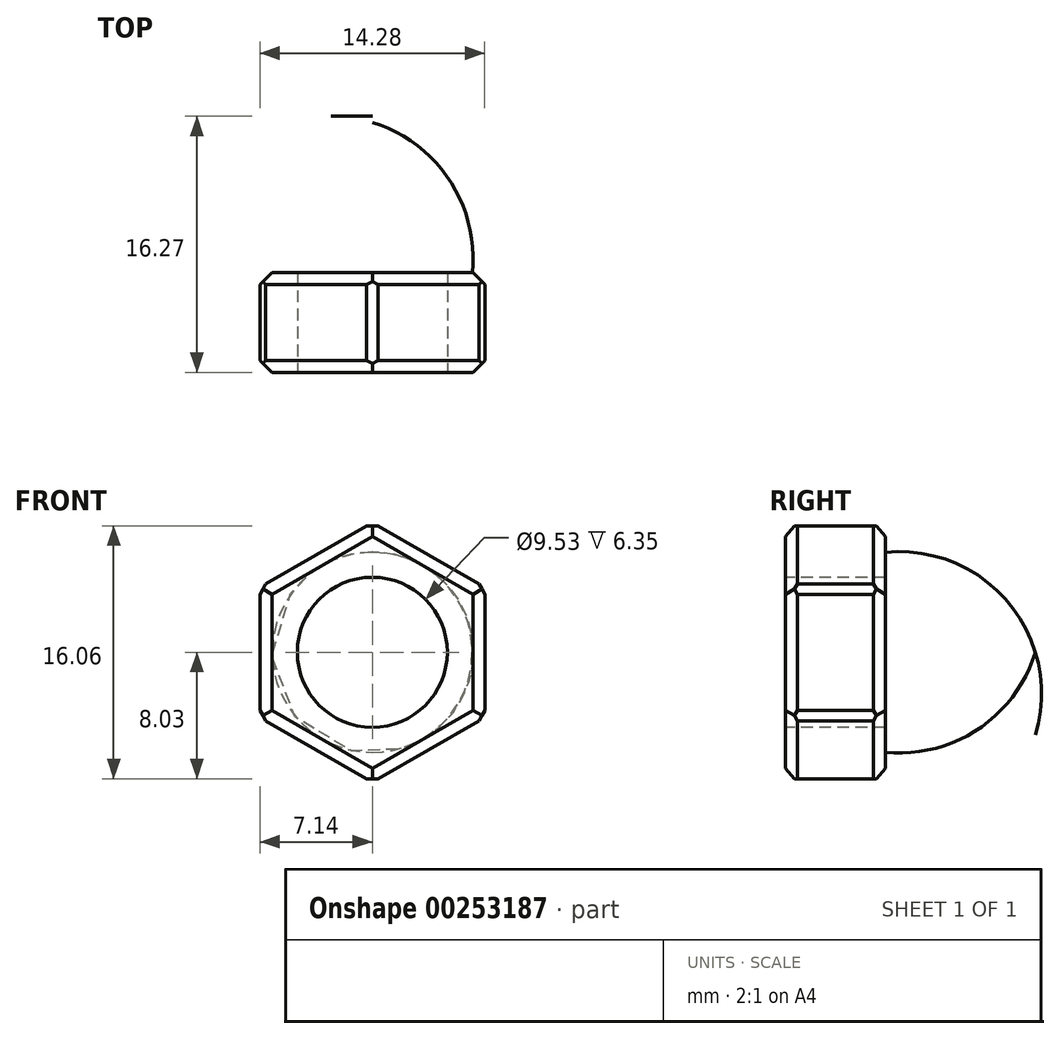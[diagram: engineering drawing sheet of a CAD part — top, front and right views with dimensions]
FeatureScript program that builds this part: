
annotation { "Feature Type Name" : "Feature", "Feature Type Description" : "" }
export const myFeature = defineFeature(function(context is Context, id is Id, definition is map)
    precondition{}
    {
        {
            var Q0;
            Q0=qCreatedBy(makeId("Front.planeOp"),FACE);
            var sketch = newSketch(context, id + "F0", { "sketchPlane" : qUnion([Q0])});
            skCircle(sketch, "E0.cCircle", {"center": v(0, 0) * mm, "radius": 7.14 * mm, "construction": true});
            skLineSegment(sketch, "E0.0", {"start": v(-7.14, -4.12) * mm, "end": v(-7.14, 4.12) * mm});
            skLineSegment(sketch, "E0.1", {"start": v(-7.14, 4.12) * mm, "end": v(0, 8.25) * mm});
            skLineSegment(sketch, "E0.2", {"start": v(0, 8.25) * mm, "end": v(7.14, 4.12) * mm});
            skLineSegment(sketch, "E0.3", {"start": v(7.14, 4.12) * mm, "end": v(7.14, -4.12) * mm});
            skLineSegment(sketch, "E0.4", {"start": v(7.14, -4.12) * mm, "end": v(0, -8.25) * mm});
            skLineSegment(sketch, "E0.5", {"start": v(0, -8.25) * mm, "end": v(-7.14, -4.12) * mm});
            skPoint(sketch, "E0.0.midPoint", {"position": v(-7.14, 0) * mm});
            skSolve(sketch);
        }
        {
            var Q0;
            Q0=makeQuery(id+"F0.imprint","IMPRINT",FACE,{"disambiguationData":[TD([[makeQuery(id+"F0.imprint","IMPRINT",EDGE,{"derivedFrom":sQuery(id+"F0.wireOp",EDGE,"E0.0")}),-1.0]])]});
            extrude(context, id + "F1", {"entities" : qUnion([Q0]), "depth" : 6.35 * mm, "symmetric" : true});
        }
        {
            var Q0;
            Q0=makeQuery(id+"F1.opExtrude","CAP_FACE",FACE,{"disambiguationData":[OSD([sQuery(id+"F0.wireOp",EDGE,"E0.0"),sQuery(id+"F0.wireOp",EDGE,"E0.1"),sQuery(id+"F0.wireOp",EDGE,"E0.2"),sQuery(id+"F0.wireOp",EDGE,"E0.3"),sQuery(id+"F0.wireOp",EDGE,"E0.4"),sQuery(id+"F0.wireOp",EDGE,"E0.5")])],"isStart":false});
            var sketch = newSketch(context, id + "F2", { "sketchPlane" : qUnion([Q0])});
            skCircle(sketch, "E1", {"center": v(0, 0) * mm, "radius": 4.76 * mm});
            skSolve(sketch);
        }
        {
            var Q0;
            Q0=qSketchRegion(id+"F2",true);
            extrude(context, id + "F3", {"entities" : qUnion([Q0]), "operationType" : NewBodyOperationType.REMOVE, "oppositeDirection" : true, "depth" : 25 * mm});
        }
        {
            var Q0;
            Q0=makeQuery(id+"F1.opExtrude","SWEPT_EDGE",EDGE,{"disambiguationData":[OSD([sQuery(id+"F0.wireOp",EDGE,"E0.1"),sQuery(id+"F0.wireOp",EDGE,"E0.2")])]});
            var Q1;
            Q1=makeQuery(id+"F1.opExtrude","SWEPT_EDGE",EDGE,{"disambiguationData":[OSD([sQuery(id+"F0.wireOp",EDGE,"E0.2"),sQuery(id+"F0.wireOp",EDGE,"E0.3")])]});
            var Q2;
            Q2=makeQuery(id+"F1.opExtrude","SWEPT_EDGE",EDGE,{"disambiguationData":[OSD([sQuery(id+"F0.wireOp",EDGE,"E0.3"),sQuery(id+"F0.wireOp",EDGE,"E0.4")])]});
            var Q3;
            Q3=makeQuery(id+"F1.opExtrude","SWEPT_EDGE",EDGE,{"disambiguationData":[OSD([sQuery(id+"F0.wireOp",EDGE,"E0.4"),sQuery(id+"F0.wireOp",EDGE,"E0.5")])]});
            var Q4;
            Q4=makeQuery(id+"F1.opExtrude","SWEPT_EDGE",EDGE,{"disambiguationData":[OSD([sQuery(id+"F0.wireOp",EDGE,"E0.0"),sQuery(id+"F0.wireOp",EDGE,"E0.5")])]});
            var Q5;
            Q5=makeQuery(id+"F1.opExtrude","SWEPT_EDGE",EDGE,{"disambiguationData":[OSD([sQuery(id+"F0.wireOp",EDGE,"E0.0"),sQuery(id+"F0.wireOp",EDGE,"E0.1")])]});
            chamfer(context, id + "F4", {"entities" : qUnion([Q0, Q1, Q2, Q3, Q4, Q5]), "width" : 0.76 * mm, "tangentPropagation" : true});
        }
        {
            var Q0;
            Q0=makeQuery(id+"F1.opExtrude","CAP_EDGE",EDGE,{"disambiguationData":[OSD([sQuery(id+"F0.wireOp",EDGE,"E0.5")])],"isStart":false});
            var Q1;
            Q1=makeQuery(id+"F1.opExtrude","CAP_EDGE",EDGE,{"disambiguationData":[OSD([sQuery(id+"F0.wireOp",EDGE,"E0.4")])],"isStart":false});
            var Q2;
            Q2=makeQuery(id+"F1.opExtrude","CAP_EDGE",EDGE,{"disambiguationData":[OSD([sQuery(id+"F0.wireOp",EDGE,"E0.3")])],"isStart":false});
            var Q3;
            Q3=makeQuery(id+"F1.opExtrude","CAP_EDGE",EDGE,{"disambiguationData":[OSD([sQuery(id+"F0.wireOp",EDGE,"E0.2")])],"isStart":false});
            var Q4;
            Q4=makeQuery(id+"F1.opExtrude","CAP_EDGE",EDGE,{"disambiguationData":[OSD([sQuery(id+"F0.wireOp",EDGE,"E0.1")])],"isStart":false});
            var Q5;
            Q5=makeQuery(id+"F1.opExtrude","CAP_EDGE",EDGE,{"disambiguationData":[OSD([sQuery(id+"F0.wireOp",EDGE,"E0.0")])],"isStart":false});
            chamfer(context, id + "F5", {"entities" : qUnion([Q0, Q1, Q2, Q3, Q4, Q5]), "width" : 0.76 * mm, "tangentPropagation" : true});
        }
        {
            var Q0;
            Q0=makeQuery(id+"F1.opExtrude","CAP_EDGE",EDGE,{"disambiguationData":[OSD([sQuery(id+"F0.wireOp",EDGE,"E0.5")])],"isStart":true});
            var Q1;
            Q1=makeQuery(id+"F1.opExtrude","CAP_EDGE",EDGE,{"disambiguationData":[OSD([sQuery(id+"F0.wireOp",EDGE,"E0.4")])],"isStart":true});
            var Q2;
            Q2=makeQuery(id+"F1.opExtrude","CAP_EDGE",EDGE,{"disambiguationData":[OSD([sQuery(id+"F0.wireOp",EDGE,"E0.3")])],"isStart":true});
            var Q3;
            Q3=makeQuery(id+"F1.opExtrude","CAP_EDGE",EDGE,{"disambiguationData":[OSD([sQuery(id+"F0.wireOp",EDGE,"E0.2")])],"isStart":true});
            var Q4;
            Q4=makeQuery(id+"F1.opExtrude","CAP_EDGE",EDGE,{"disambiguationData":[OSD([sQuery(id+"F0.wireOp",EDGE,"E0.1")])],"isStart":true});
            var Q5;
            Q5=makeQuery(id+"F1.opExtrude","CAP_EDGE",EDGE,{"disambiguationData":[OSD([sQuery(id+"F0.wireOp",EDGE,"E0.0")])],"isStart":true});
            chamfer(context, id + "F6", {"entities" : qUnion([Q0, Q1, Q2, Q3, Q4, Q5]), "width" : 0.76 * mm, "tangentPropagation" : true});
        }
        {
            var Q0;
            Q0=qCreatedBy(makeId("Top.planeOp"),FACE);
            var sketch = newSketch(context, id + "F7", { "sketchPlane" : qUnion([Q0])});
            skLineSegment(sketch, "E2", {"start": v(0, 3.18) * mm, "end": v(0, 12.7) * mm});
            skLineSegment(sketch, "E3", {"start": v(0, 3.18) * mm, "end": v(6.35, 3.18) * mm});
            skArc(sketch, "E4", {"start": v(6.35, 3.18) * mm, "mid": v(4.88, 9.07) * mm, "end": v(0, 12.7) * mm});
            skSolve(sketch);
        }
        {
            var Q0;
            Q0=makeQuery(id+"F7.imprint","IMPRINT",FACE,{"disambiguationData":[TD([[makeQuery(id+"F7.imprint","IMPRINT",EDGE,{"derivedFrom":sQuery(id+"F7.wireOp",EDGE,"E2")}),-1.0]])]});
            var Q1;
            Q1=sQuery(id+"F7.wireOp",EDGE,"E2");
            revolve(context, id + "F8", {"operationType" : NewBodyOperationType.ADD, "entities" : qUnion([Q0]), "axis" : qUnion([Q1]), "revolveType" : RevolveType.FULL});
        }
    });
